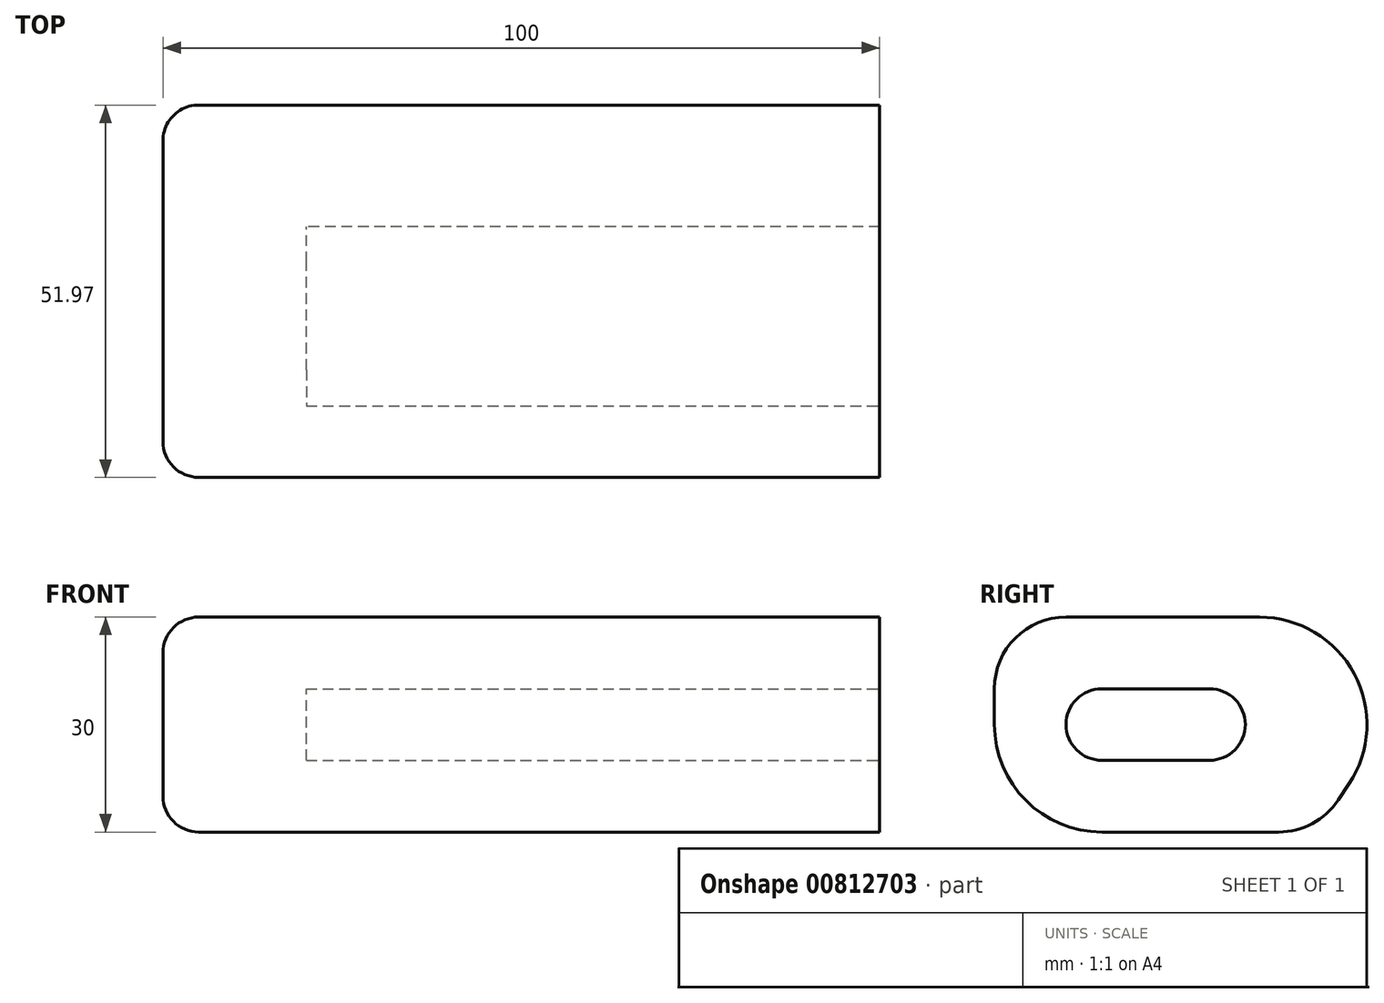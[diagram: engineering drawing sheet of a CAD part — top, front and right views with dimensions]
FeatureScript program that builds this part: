
annotation { "Feature Type Name" : "Feature", "Feature Type Description" : "" }
export const myFeature = defineFeature(function(context is Context, id is Id, definition is map)
    precondition{}
    {
        {
            var Q0;
            Q0=qCreatedBy(makeId("Right.planeOp"),FACE);
            var sketch = newSketch(context, id + "F0", { "sketchPlane" : qUnion([Q0])});
            skLineSegment(sketch, "E0", {"start": v(0, 0) * mm, "end": v(65, 0) * mm});
            skLineSegment(sketch, "E1", {"start": v(0, 0) * mm, "end": v(0, -30) * mm});
            skLineSegment(sketch, "E2", {"start": v(0, -30) * mm, "end": v(45, -30) * mm});
            skLineSegment(sketch, "E3", {"start": v(45, -30) * mm, "end": v(65, 0) * mm});
            skSolve(sketch);
        }
        {
            var Q0;
            Q0=makeQuery(id+"F0.imprint","IMPRINT",FACE,{"disambiguationData":[TD([[makeQuery(id+"F0.imprint","IMPRINT",EDGE,{"derivedFrom":sQuery(id+"F0.wireOp",EDGE,"E0")}),-1.0]])]});
            extrude(context, id + "F1", {"entities" : qUnion([Q0]), "depth" : 100 * mm, "offsetDistance" : 25 * mm});
        }
        {
            var Q0;
            Q0=makeQuery(id+"F1.opExtrude","SWEPT_EDGE",EDGE,{"disambiguationData":[OSD([sQuery(id+"F0.wireOp",EDGE,"E0"),sQuery(id+"F0.wireOp",EDGE,"E3")])]});
            var Q1;
            Q1=makeQuery(id+"F1.opExtrude","SWEPT_EDGE",EDGE,{"disambiguationData":[OSD([sQuery(id+"F0.wireOp",EDGE,"E1"),sQuery(id+"F0.wireOp",EDGE,"E2")])]});
            fillet(context, id + "F2", {"entities" : qUnion([Q0, Q1]), "radius" : 15 * mm, "tangentPropagation" : true, "allowEdgeOverflow" : false});
        }
        {
            var Q0;
            Q0=makeQuery(id+"F1.opExtrude","CAP_FACE",FACE,{"disambiguationData":[OSD([sQuery(id+"F0.wireOp",EDGE,"E0"),sQuery(id+"F0.wireOp",EDGE,"E1"),sQuery(id+"F0.wireOp",EDGE,"E2"),sQuery(id+"F0.wireOp",EDGE,"E3")])],"isStart":false});
            var sketch = newSketch(context, id + "F3", { "sketchPlane" : qUnion([Q0])});
            skLineSegment(sketch, "E4", {"start": v(45, 20.43) * mm, "end": v(45, -66.08) * mm});
            skLineSegment(sketch, "E5", {"start": v(-12.57, -10) * mm, "end": v(97.75, -10) * mm});
            skLineSegment(sketch, "E6", {"start": v(0, 26.68) * mm, "end": v(0, -52.25) * mm});
            skLineSegment(sketch, "E7", {"start": v(-5.47, 0) * mm, "end": v(61.04, 0) * mm});
            skLineSegment(sketch, "E8", {"start": v(35, 18.14) * mm, "end": v(35, -42.63) * mm});
            skLineSegment(sketch, "E9", {"start": v(10, 19.18) * mm, "end": v(10, -47.07) * mm});
            skLineSegment(sketch, "E10", {"start": v(22.2, -30) * mm, "end": v(-18.61, -30) * mm});
            skLineSegment(sketch, "E11", {"start": v(-11.52, -20) * mm, "end": v(81.72, -20) * mm});
            skSolve(sketch);
        }
        {
            var Q0;
            {var subQ0=sQuery(id+"F3.wireOp",EDGE,"E9");var subQ1=sQuery(id+"F3.wireOp",EDGE,"E5");var subQ2=makeQuery(id+"F3.imprint","INTERSECT",VERTEX,{"derivedFrom":[subQ1,subQ0]});Q0=makeQuery(id+"F3.imprint","IMPRINT",FACE,{"disambiguationData":[TD([[makeQuery(id+"F3.imprint","IMPRINT",EDGE,{"disambiguationData":[TD([[subQ2,-1.0]])],"derivedFrom":subQ1}),-1.0]])]});}
            extrude(context, id + "F4", {"entities" : qUnion([Q0]), "operationType" : NewBodyOperationType.REMOVE, "oppositeDirection" : true, "depth" : 80 * mm, "offsetDistance" : 25 * mm});
        }
        {
            var Q0;
            Q0=makeQuery(id+"F4.boolean.opBoolean","COPY",EDGE,{"derivedFrom":makeQuery(id+"F4.opExtrude","SWEPT_EDGE",EDGE,{"disambiguationData":[OSD([sQuery(id+"F3.wireOp",EDGE,"E5"),sQuery(id+"F3.wireOp",EDGE,"E9")])]})});
            var Q1;
            Q1=makeQuery(id+"F4.boolean.opBoolean","COPY",EDGE,{"derivedFrom":makeQuery(id+"F4.opExtrude","SWEPT_EDGE",EDGE,{"disambiguationData":[OSD([sQuery(id+"F3.wireOp",EDGE,"E9"),sQuery(id+"F3.wireOp",EDGE,"E11")])]})});
            var Q2;
            Q2=makeQuery(id+"F4.boolean.opBoolean","COPY",EDGE,{"derivedFrom":makeQuery(id+"F4.opExtrude","SWEPT_EDGE",EDGE,{"disambiguationData":[OSD([sQuery(id+"F3.wireOp",EDGE,"E5"),sQuery(id+"F3.wireOp",EDGE,"E8")])]})});
            var Q3;
            Q3=makeQuery(id+"F4.boolean.opBoolean","COPY",EDGE,{"derivedFrom":makeQuery(id+"F4.opExtrude","SWEPT_EDGE",EDGE,{"disambiguationData":[OSD([sQuery(id+"F3.wireOp",EDGE,"E8"),sQuery(id+"F3.wireOp",EDGE,"E11")])]})});
            fillet(context, id + "F5", {"entities" : qUnion([Q0, Q1, Q2, Q3]), "radius" : 5 * mm, "tangentPropagation" : true, "allowEdgeOverflow" : false});
        }
        {
            var Q0;
            Q0=makeQuery(id+"F1.opExtrude","SWEPT_EDGE",EDGE,{"disambiguationData":[OSD([sQuery(id+"F0.wireOp",EDGE,"E0"),sQuery(id+"F0.wireOp",EDGE,"E1")])]});
            var Q1;
            Q1=makeQuery(id+"F1.opExtrude","SWEPT_EDGE",EDGE,{"disambiguationData":[OSD([sQuery(id+"F0.wireOp",EDGE,"E2"),sQuery(id+"F0.wireOp",EDGE,"E3")])]});
            fillet(context, id + "F6", {"entities" : qUnion([Q0, Q1]), "radius" : 10 * mm, "tangentPropagation" : true, "allowEdgeOverflow" : false});
        }
        {
            var Q0;
            Q0=makeQuery(id+"F1.opExtrude","CAP_EDGE",EDGE,{"disambiguationData":[OSD([sQuery(id+"F0.wireOp",EDGE,"E0")])],"isStart":true});
            fillet(context, id + "F7", {"entities" : qUnion([Q0]), "radius" : 5 * mm, "tangentPropagation" : true, "allowEdgeOverflow" : false});
        }
    });
